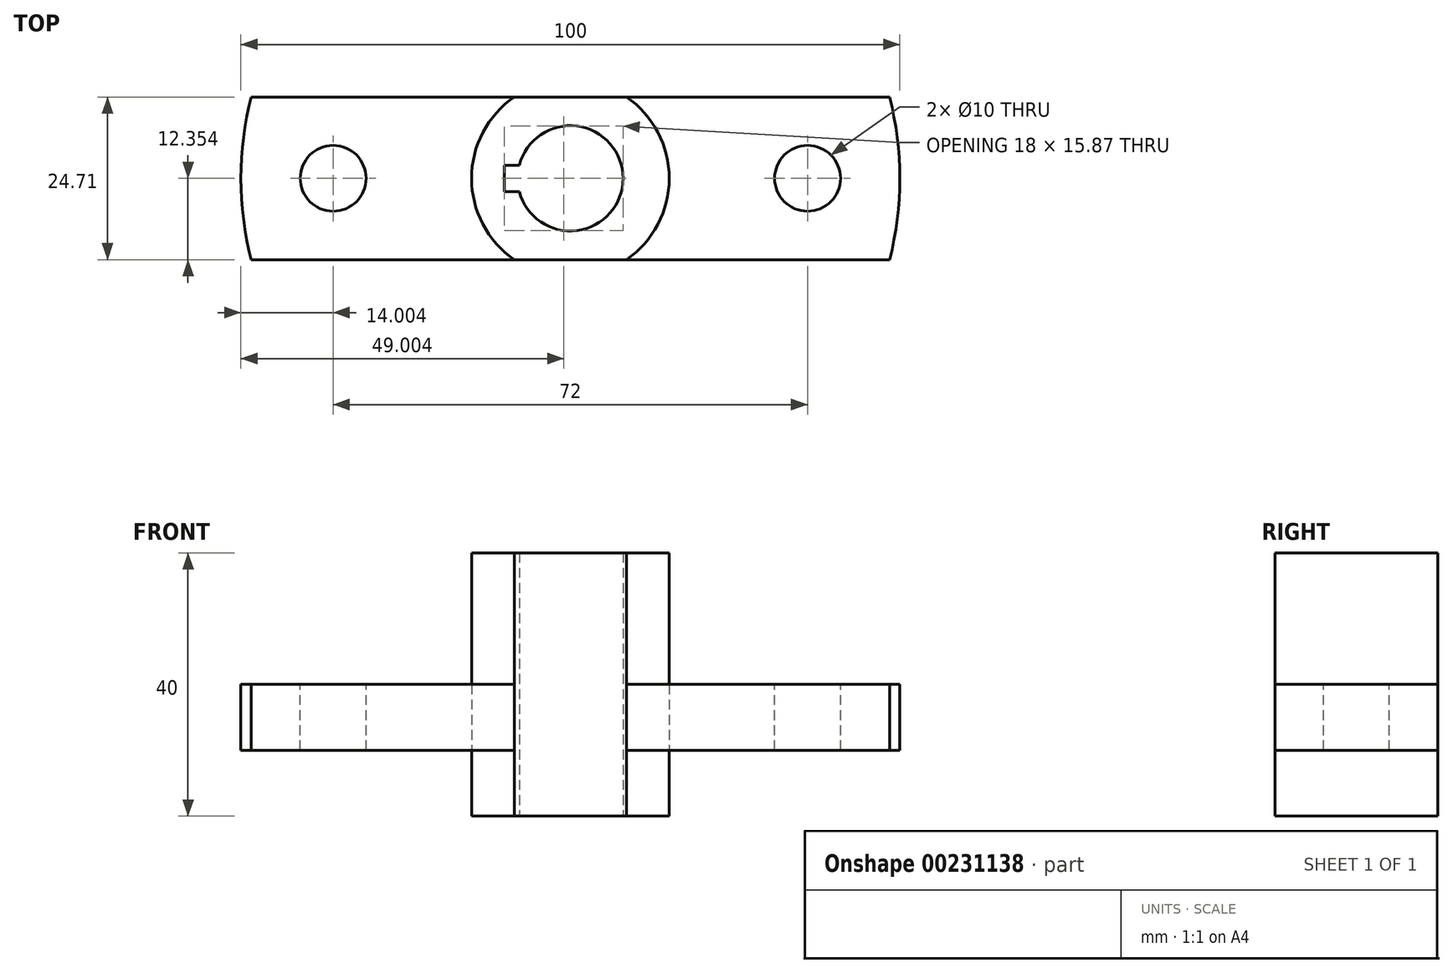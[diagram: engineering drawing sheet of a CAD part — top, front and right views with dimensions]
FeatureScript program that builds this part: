
annotation { "Feature Type Name" : "Feature", "Feature Type Description" : "" }
export const myFeature = defineFeature(function(context is Context, id is Id, definition is map)
    precondition{}
    {
        {
            var Q0;
            Q0=qCreatedBy(makeId("Top.planeOp"),FACE);
            var sketch = newSketch(context, id + "F0", { "sketchPlane" : qUnion([Q0])});
            skLineSegment(sketch, "E0.bottom", {"start": v(-5.45, -2.11) * mm, "end": v(91.44, -2.11) * mm});
            skLineSegment(sketch, "E0.top", {"start": v(-5.45, 22.6) * mm, "end": v(91.44, 22.6) * mm});
            skLineSegment(sketch, "E1", {"start": v(-7.04, 10.24) * mm, "end": v(93.03, 10.24) * mm, "construction": true});
            skCircle(sketch, "E2", {"center": v(43, 10.24) * mm, "radius": 8 * mm});
            skArc(sketch, "E3", {"start": v(34.5, 22.6) * mm, "mid": v(28, 10.24) * mm, "end": v(34.5, -2.11) * mm});
            skCircle(sketch, "E4", {"center": v(7, 10.24) * mm, "radius": 5 * mm});
            skCircle(sketch, "E5", {"center": v(79, 10.24) * mm, "radius": 5 * mm});
            skArc(sketch, "E6", {"start": v(-5.45, 22.6) * mm, "mid": v(-7, 10.24) * mm, "end": v(-5.45, -2.11) * mm});
            skArc(sketch, "E7.trimOffspring", {"start": v(51.5, -2.11) * mm, "mid": v(58, 10.24) * mm, "end": v(51.5, 22.6) * mm});
            skLineSegment(sketch, "E8", {"start": v(35.25, 12.24) * mm, "end": v(33, 12.24) * mm});
            skLineSegment(sketch, "E9", {"start": v(33, 12.24) * mm, "end": v(33, 8.24) * mm});
            skLineSegment(sketch, "E10", {"start": v(33, 8.24) * mm, "end": v(35.25, 8.24) * mm});
            skArc(sketch, "E11.trimOffspring", {"start": v(91.44, -2.11) * mm, "mid": v(93, 10.24) * mm, "end": v(91.44, 22.6) * mm});
            skSolve(sketch);
        }
        {
            var Q0;
            Q0=makeQuery(id+"F0.imprint","IMPRINT",FACE,{"disambiguationData":[TD([[makeQuery(id+"F0.imprint","IMPRINT",EDGE,{"derivedFrom":sQuery(id+"F0.wireOp",EDGE,"E5")}),-1.0]])]});
            var Q1;
            {var subQ0=sQuery(id+"F0.wireOp",EDGE,"E3");Q1=makeQuery(id+"F0.imprint","IMPRINT",FACE,{"disambiguationData":[TD([[makeQuery(id+"F0.imprint","IMPRINT",EDGE,{"derivedFrom":subQ0}),-1.0]])]});}
            extrude(context, id + "F1", {"entities" : qUnion([Q0, Q1]), "oppositeDirection" : true, "depth" : 10 * mm});
        }
        {
            var Q0;
            {var subQ0=sQuery(id+"F0.wireOp",EDGE,"E3");Q0=makeQuery(id+"F0.imprint","IMPRINT",FACE,{"disambiguationData":[TD([[makeQuery(id+"F0.imprint","IMPRINT",EDGE,{"derivedFrom":subQ0}),1.0]])]});}
            extrude(context, id + "F2", {"entities" : qUnion([Q0]), "endBound" : BoundingType.SYMMETRIC, "depth" : 40 * mm});
        }
    });
